# Revit family: BC_RHME-(80-90)AH2_LOD400_
name_source: partatom
category: Equipement de génie climatique
revit_build: Autodesk Revit 2017 (Build: 20160225_1515(x64)
units: mm (PartAtom-declared; Revit-internal decimal feet)

## family parameters
Basée sur le plan de construction = Non
Cote de connecteur circulaire = Utiliser le diamètre
Couper avec des vides une fois chargée = Non
Numéro OmniClass = 23.75.10.24
Partagée = Non
Point de calcul de pièce = Non
Titre OmniClass = Cooling and Freeze Plant
Toujours verticalement = Oui
Type d'élément = Normal

## types (2) — shared parameters
Coefficient Of Performance (COP) = 2.84
Color = Natural Grey
Description = Samurai - Air Cooled Heat Pump
Fabricant = HITACHI
Heating Nominal Current = 107 A
Heating Nominal Flow = 31.8 m³/h
Heating Nominal Input Power = 65 kW
Heating Power = 65 kW
Heating Pressure Drop at nominal flow = 13.7 kPa
Inlet Water Diameter = 368 mm
Maximum AC Voltage = 440 V
Maximum Air Flow = 75.6 m³/h
Maximum Starting Current for cable sizing = 240 A
Minimum AC Voltage = 360 V
Modèle = Samurai - Air Cooled Heat Pump
Nominal Voltage = 400 V
Operating Mode Heat Pump = Heat Pump (5)
Overall Height = 2450 mm
Overall Length = 3230 mm
Overall Width = 1955 mm
Rated Frequency = 50 Hz
Refrigerant Quantity = 49.00 kg
Refrigerant Type = R134a
Season Coefficient Of Performance (SCOP) = 3.25
Starting Current = 240 A
Static Pressure = 0.0 kPa
Water Outlet Diameter = 368 mm

## per-type parameters (varying)
- Samurai - Air Cooled Heat Pump - RHME 80AH2: AXI_PDS_FCT=1680.00 kg; Cooling Airflow High=47.9 m³/h; Cooling Capacity=195 kW; Cooling Capacity Min=21 kW; Cooling Nominal Current=108 A; Cooling Nominal Flow=33.5 m³/h; Cooling Nominal Input Power=66 kW; Cooling Power=66 kW; Cooling Pressure Drop at nominal flow=15.1 kPa; Energy Efficiency Ratio (EER)=2.95; Extra Super Low Noise Model (dB(A))=90; Extra Super Low Noise Model at 10m (dB(A))=62; Heating Airflow High=47.9 m³/h; Heating Capacity=185 kW; Heating Capacity Min=21 kW; Heating Sound Level Low (dB)=95; Heating Sound Level Silent (dB)=98; Low Noise Model at 10m (dB(A))=67; Maximum Current for cable sizing=140 A; Maximum Input Power for cable sizing=82 kW; Product Code=9E081342; Seasonal Energy Efficiency Ratio (SEER)=3.92; Standard Noise Level Model at 10m (dB(A))=70; Super Low Noise Model (dB(A))=93; Super Low Noise Model at 10m (dB(A))=65; Weight Packing=1660.00 kg
- Samurai - Air Cooled Heat Pump - RHME 90AH2: AXI_PDS_FCT=1760.00 kg; Cooling Airflow High=51.6 m³/h; Cooling Capacity=210 kW; Cooling Capacity Min=23 kW; Cooling Nominal Current=115 A; Cooling Nominal Flow=36.1 m³/h; Cooling Nominal Input Power=70 kW; Cooling Power=70 kW; Cooling Pressure Drop at nominal flow=17.3 kPa; Energy Efficiency Ratio (EER)=2.98; Extra Super Low Noise Model (dB(A))=91; Extra Super Low Noise Model at 10m (dB(A))=63; Heating Airflow High=51.6 m³/h; Heating Capacity=186 kW; Heating Capacity Min=23 kW; Heating Sound Level Low (dB)=96; Heating Sound Level Silent (dB)=99; Low Noise Model at 10m (dB(A))=68; Maximum Current for cable sizing=143 A; Maximum Input Power for cable sizing=84 kW; Product Code=9E091342; Seasonal Energy Efficiency Ratio (SEER)=3.96; Standard Noise Level Model at 10m (dB(A))=71; Super Low Noise Model (dB(A))=94; Super Low Noise Model at 10m (dB(A))=66; Weight Packing=1740.00 kg

note: column(s) folded — value = type name in every type: Commentaires du type
